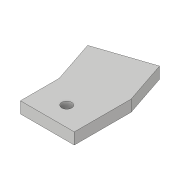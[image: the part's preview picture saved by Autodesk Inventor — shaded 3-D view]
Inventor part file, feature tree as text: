
AUTODESK INVENTOR PART (.ipt)
format: ipt  version: 2018.3 (Build 223284000, 284)  size: 114,176 bytes
history: native  units: in
note: dims shown in document units (in); Inventor stores cm internally (conversion verified against a paired STEP export)
features: extrude x2, fillet x1, sketch x1
ambient origin geometry x8: Origin, YZ Plane, XZ Plane, XY Plane, X Axis, Y Axis, Z Axis, Center Point
bodies: Solid1 (feature_tree)
feature tree (4):
  extrude  "Extrusion1"  Depth=0.875in
  extrude  "Extrusion2"  Depth=1.1003in
  fillet  "Fillet1"  Radius=1.0432in
  sketch  "Sketch1"  dims[d0=0.75in d1=0.875in d2=1.1003in d3=1.0432in d4=0.1925in d5=0.221in d6=0.0in d7=0.0625in d8=0.0in d15=0.126in d16=0.125in d17=0.126in d18=0.5216in d19=0.375in d20=1.1095in d21=0.0625in]
